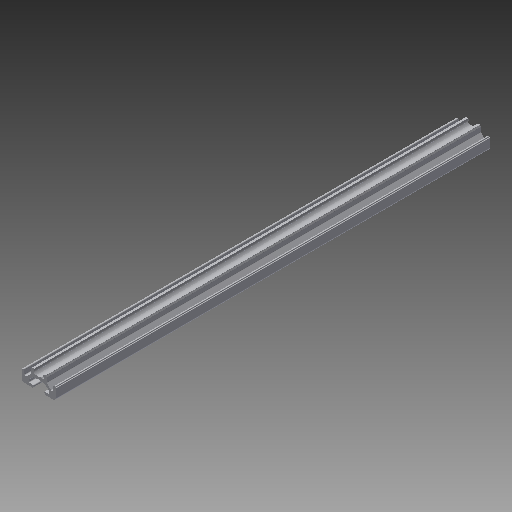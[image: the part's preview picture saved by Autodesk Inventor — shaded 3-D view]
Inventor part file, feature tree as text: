
AUTODESK INVENTOR PART (.ipt)
format: ipt  version: 2017 (Build 210142000, 142)  size: 346,112 bytes
history: native  units: in
note: dims shown in document units (in); Inventor stores cm internally (conversion verified against a paired STEP export)
features: other x3, extrude x2, sketch x2, thicken_offset x1
ambient origin geometry x8: Origin, YZ Plane, XZ Plane, XY Plane, X Axis, Y Axis, Z Axis, Center Point
bodies: Solid1 (feature_tree)
feature tree (8):
  other  "Blocks"
  extrude  "Extrusion1"  Depth=4.5in
  thicken_offset  "Thicken1"
  extrude  "Extrusion3"  Depth=0.3935in TaperAngle=0.0deg
  sketch  "Sketch1"  dims[d1=0.0in d5=4.5in]
  other  "20x20"
  sketch  "Sketch3"  dims[d6=4.5in d7=0.3935in d8=0.0in]
  other  "20x20:1"
